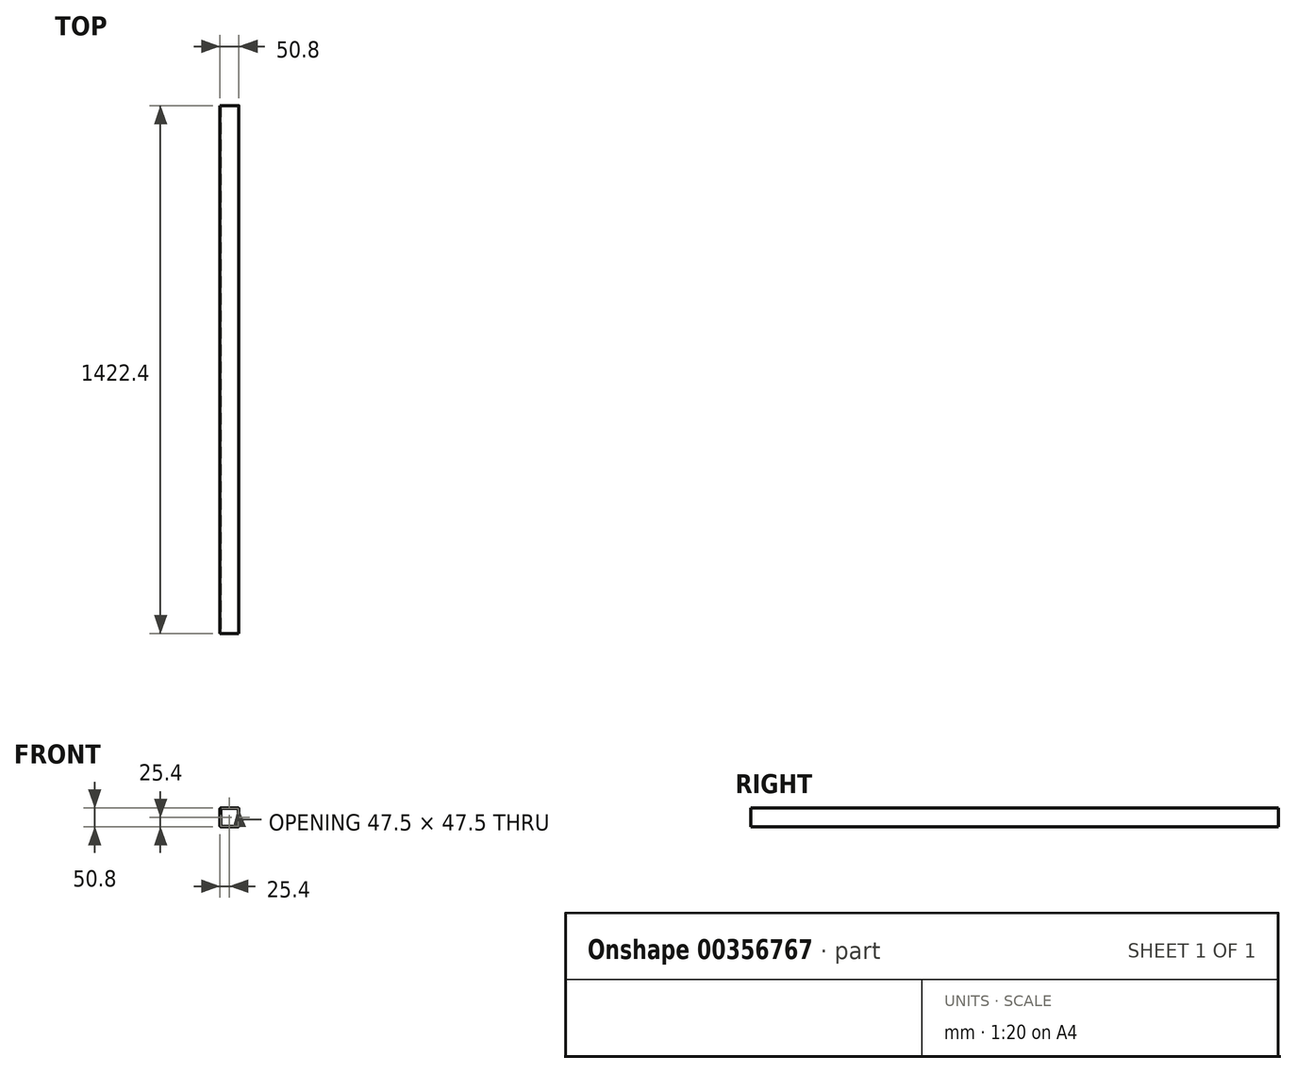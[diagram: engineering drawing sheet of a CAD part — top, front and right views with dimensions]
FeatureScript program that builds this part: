
annotation { "Feature Type Name" : "Feature", "Feature Type Description" : "" }
export const myFeature = defineFeature(function(context is Context, id is Id, definition is map)
    precondition{}
    {
        {
            var Q0;
            Q0=qCreatedBy(makeId("Front.planeOp"),FACE);
            var sketch = newSketch(context, id + "F0", { "sketchPlane" : qUnion([Q0])});
            skLineSegment(sketch, "E0.bottom", {"start": v(25.4, -25.4) * mm, "end": v(-25.4, -25.4) * mm});
            skLineSegment(sketch, "E0.top", {"start": v(25.4, 25.4) * mm, "end": v(-25.4, 25.4) * mm});
            skLineSegment(sketch, "E0.left", {"start": v(25.4, -25.4) * mm, "end": v(25.4, 25.4) * mm});
            skLineSegment(sketch, "E0.right", {"start": v(-25.4, -25.4) * mm, "end": v(-25.4, 25.4) * mm});
            skPoint(sketch, "E0.middle", {"position": v(0, 0) * mm});
            skLineSegment(sketch, "E1.bottom", {"start": v(23.75, -23.75) * mm, "end": v(-23.75, -23.75) * mm});
            skLineSegment(sketch, "E1.top", {"start": v(23.75, 23.75) * mm, "end": v(-23.75, 23.75) * mm});
            skLineSegment(sketch, "E1.left", {"start": v(23.75, -23.75) * mm, "end": v(23.75, 23.75) * mm});
            skLineSegment(sketch, "E1.right", {"start": v(-23.75, -23.75) * mm, "end": v(-23.75, 23.75) * mm});
            skSolve(sketch);
        }
        {
            var Q0;
            Q0=makeQuery(id+"F0.imprint","IMPRINT",FACE,{"disambiguationData":[TD([[makeQuery(id+"F0.imprint","IMPRINT",EDGE,{"derivedFrom":sQuery(id+"F0.wireOp",EDGE,"E0.bottom")}),-1.0]])]});
            extrude(context, id + "F1", {"entities" : qUnion([Q0]), "oppositeDirection" : true, "depth" : 1422.4 * mm});
        }
        {
            var Q0;
            Q0=makeQuery(id+"F1.opExtrude","SWEPT_EDGE",EDGE,{"disambiguationData":[OSD([sQuery(id+"F0.wireOp",EDGE,"E1.top"),sQuery(id+"F0.wireOp",EDGE,"E1.right")])]});
            var Q1;
            Q1=makeQuery(id+"F1.opExtrude","SWEPT_EDGE",EDGE,{"disambiguationData":[OSD([sQuery(id+"F0.wireOp",EDGE,"E1.top"),sQuery(id+"F0.wireOp",EDGE,"E1.left")])]});
            var Q2;
            Q2=makeQuery(id+"F1.opExtrude","SWEPT_EDGE",EDGE,{"disambiguationData":[OSD([sQuery(id+"F0.wireOp",EDGE,"E1.bottom"),sQuery(id+"F0.wireOp",EDGE,"E1.right")])]});
            var Q3;
            Q3=makeQuery(id+"F1.opExtrude","SWEPT_EDGE",EDGE,{"disambiguationData":[OSD([sQuery(id+"F0.wireOp",EDGE,"E1.bottom"),sQuery(id+"F0.wireOp",EDGE,"E1.left")])]});
            fillet(context, id + "F2", {"entities" : qUnion([Q0, Q1, Q2, Q3]), "radius" : 1.65 * mm, "tangentPropagation" : true, "allowEdgeOverflow" : false});
        }
        {
            var Q0;
            Q0=makeQuery(id+"F1.opExtrude","SWEPT_EDGE",EDGE,{"disambiguationData":[OSD([sQuery(id+"F0.wireOp",EDGE,"E0.top"),sQuery(id+"F0.wireOp",EDGE,"E0.right")])]});
            var Q1;
            Q1=makeQuery(id+"F1.opExtrude","SWEPT_EDGE",EDGE,{"disambiguationData":[OSD([sQuery(id+"F0.wireOp",EDGE,"E0.bottom"),sQuery(id+"F0.wireOp",EDGE,"E0.right")])]});
            var Q2;
            Q2=makeQuery(id+"F1.opExtrude","SWEPT_EDGE",EDGE,{"disambiguationData":[OSD([sQuery(id+"F0.wireOp",EDGE,"E0.top"),sQuery(id+"F0.wireOp",EDGE,"E0.left")])]});
            var Q3;
            Q3=makeQuery(id+"F1.opExtrude","SWEPT_EDGE",EDGE,{"disambiguationData":[OSD([sQuery(id+"F0.wireOp",EDGE,"E0.bottom"),sQuery(id+"F0.wireOp",EDGE,"E0.left")])]});
            fillet(context, id + "F3", {"entities" : qUnion([Q0, Q1, Q2, Q3]), "radius" : 1.65 * mm, "tangentPropagation" : true, "allowEdgeOverflow" : false});
        }
    });
